# Revit family: Drinking_Fountain-Haws_Corporation-Wall_Mounted_1109 new
name_source: partatom
category: Plumbing Fixtures
revit_build: Autodesk Revit Architecture 2015 (Build: 20160512_1515(x64)
units: mm (PartAtom-declared; Revit-internal decimal feet)

## types (8) — shared parameters
Assembly Code = D2010810
Back Plate = Metal - Haws Corporation - Stainless Steel - Satin BP3
Bowl = Metal - Haws Corporation - Stainless Steel - Satin BP3
Bowl Width = 1' - 3"
CW Connection = Yes
Cost Note = For Cost information please visit the Resource tab in the Product Page URL
Default Elevation = 0' - 0 9/16"
Flow = 0 GPM
Keynote = 15410.A1
Manufacturer = Haws Corporation
MasterFormat 2004 = 22 47 00,22 47 13,22 52 00,22 52 13
OmniClass 23 = 23-65 70 14,23-65 70 14 11,23-65 70 14 11 11
Product Documentation Link = https://www.hawsco.com
Product Page URL = http://www.hawsco.com
Revisions Date = 06/02/2009
Sanitary Radius = 0' - 0 5/8"
Series = The Haws 1109 heavy duty barrier free drinking fountain uses a patented push-button valve assembly
Supply Radius = 0' - 0 1/4"
Trim = Metal - Haws Corporation - Stainless Steel - Satin BP3
Tubing = Metal - Haws Corporation - Copper Poly
URL = http://www.hawsco.com
Version = 2014-v2.0a
zero-valued in all types: Cost, HWFU

## per-type parameters (varying)
| type | Button | CWFU | Description | FR Button | HW Connection | Trim Plate | Type Comments | Vent Connection | WFU | Waste Connection |
| 1109 | Yes | 1 | 18 gauge Type 304 Stainless Steel design without back panel | No | No | No | Placed securely in multiple locations without taking up excess space | Yes | 0 | No |
| 1109.14 | Yes | 1 | 14 gauge Type 304 Stainless Steel design without back panel | No | No | No | Placed securely in multiple locations without taking up excess space | Yes | 0 | No |
| 1109A | Yes | 1 | 18 gauge Type 304 Stainless Steel design without back panel | No | No | No | Fountain with antimicrobial protection* uses a patented push-button valve assembly | Yes | 0 | No |
| 1109BP | Yes | 1 | Design with matching back panel | No | No | No | Placed securely in multiple locations without taking up excess space | Yes | 1 | Yes |
| 1109FR | No | 1 | Fountain uses a fully engineered pneumatic operated freeze-resistant valve assembly for continual use during winter months | Yes | No | No | Without Back Panel, wall mounted, barrier-free, stainless steel drinking fountain with satin finish | Yes | 0 | No |
| 1109FRBP | No | 1 | Fountain uses a fully engineered pneumatic operated freeze-resistant valve assembly for continual use during winter months | Yes | No | No | Design with matching back panel, wall mounted, barrier-free, stainless steel drinking fountain with satin finish | Yes | 1 | Yes |
| H1109.8 | Yes | 2 | Designed to run at a low energy usage, this water cooler and fountain are assured to have a long lasting life | No | Yes | Yes | Electric drinking fountain provides 8 gph chilled water | No | 1 | Yes |
| H1109.8A | Yes | 2 | Designed to run at a low energy usage, this water cooler and fountain are assured to have a long lasting life | No | Yes | Yes | Electric drinking fountain with antimicrobial protection* provides 8 gph chilled water | No | 1 | Yes |

note: column(s) folded — value = type name in every type: Model

## geometry (parser evidence)
native form markers: Blend x12, Sweep x8
no freeform markers — native parametric forms only
